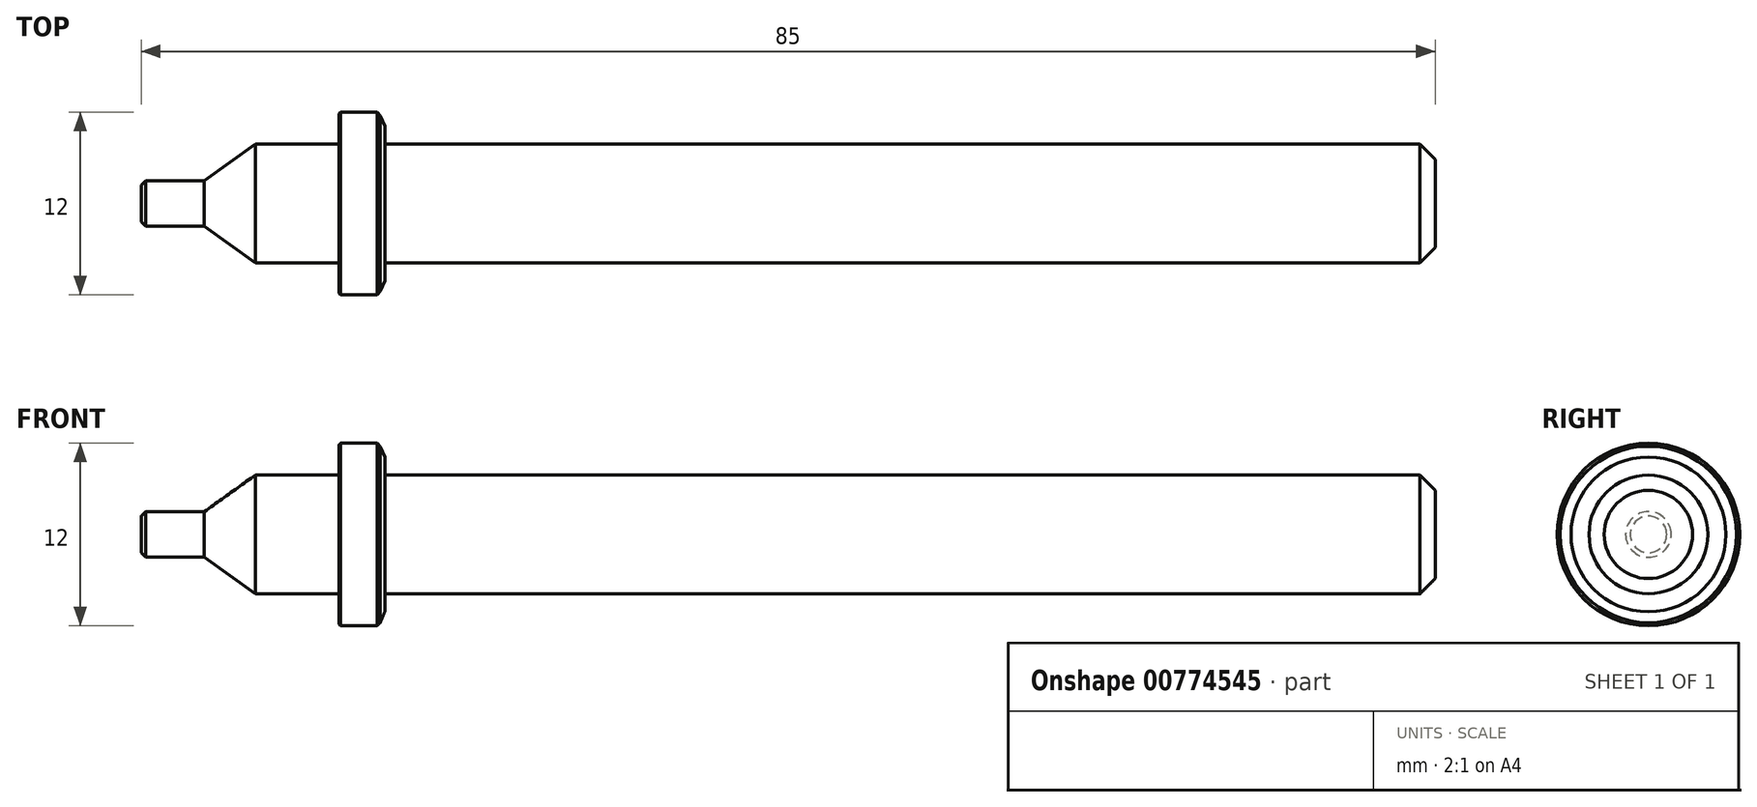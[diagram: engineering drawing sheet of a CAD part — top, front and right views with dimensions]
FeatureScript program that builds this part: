
annotation { "Feature Type Name" : "Feature", "Feature Type Description" : "" }
export const myFeature = defineFeature(function(context is Context, id is Id, definition is map)
    precondition{}
    {
        {
            var Q0;
            Q0=qCreatedBy(makeId("Front.planeOp"),FACE);
            var sketch = newSketch(context, id + "F0", { "sketchPlane" : qUnion([Q0])});
            skLineSegment(sketch, "E0", {"start": v(0, 0) * mm, "end": v(30.28, 0) * mm, "construction": true});
            skLineSegment(sketch, "E1", {"start": v(0, 0) * mm, "end": v(0, 1.5) * mm});
            skLineSegment(sketch, "E2", {"start": v(0, 1.5) * mm, "end": v(4.15, 1.5) * mm});
            skLineSegment(sketch, "E3", {"start": v(4.15, 1.5) * mm, "end": v(7.5, 3.9) * mm});
            skLineSegment(sketch, "E4", {"start": v(7.5, 3.9) * mm, "end": v(13, 3.9) * mm});
            skLineSegment(sketch, "E5", {"start": v(13, 3.9) * mm, "end": v(13, 6) * mm});
            skLineSegment(sketch, "E6", {"start": v(13, 6) * mm, "end": v(16, 6) * mm});
            skLineSegment(sketch, "E7", {"start": v(16, 6) * mm, "end": v(16, 3.9) * mm});
            skLineSegment(sketch, "E8", {"start": v(85, 3.9) * mm, "end": v(85, 0) * mm});
            skLineSegment(sketch, "E9", {"start": v(71, 3.9) * mm, "end": v(71, 0) * mm});
            skLineSegment(sketch, "E10", {"start": v(16, 3.9) * mm, "end": v(71, 3.9) * mm});
            skLineSegment(sketch, "E11", {"start": v(71, 3.9) * mm, "end": v(85, 3.9) * mm});
            skLineSegment(sketch, "E12", {"start": v(0, 0) * mm, "end": v(71, 0) * mm});
            skLineSegment(sketch, "E13", {"start": v(71, 0) * mm, "end": v(85, 0) * mm});
            skSolve(sketch);
        }
        {
            var Q0;
            Q0 = qSketchRegion(id + "F0", true);
            var Q1;
            Q1=sQuery(id+"F0.wireOp",EDGE,"E12");
            revolve(context, id + "F1", {"surfaceOperationType" : NewSurfaceOperationType.NEW, "entities" : qUnion([Q0]), "axis" : qUnion([Q1]), "revolveType" : RevolveType.FULL});
        }
        {
            var Q0;
            Q0=makeQuery(id+"F1.opRevolve","SWEPT_EDGE",EDGE,{"disambiguationData":[OSD([sQuery(id+"F0.wireOp",EDGE,"E6"),sQuery(id+"F0.wireOp",EDGE,"E7")])]});
            chamfer(context, id + "F2", {"entities" : qUnion([Q0]), "width" : 0.5 * mm, "tangentPropagation" : true});
        }
        {
            var Q0;
            Q0=makeQuery(id+"F1.opRevolve","SWEPT_EDGE",EDGE,{"disambiguationData":[OSD([sQuery(id+"F0.wireOp",EDGE,"E5"),sQuery(id+"F0.wireOp",EDGE,"E6")])]});
            chamfer(context, id + "F3", {"entities" : qUnion([Q0]), "width" : 0.1 * mm, "tangentPropagation" : true});
        }
        {
            var Q0;
            Q0=makeQuery(id+"F1.opRevolve","SWEPT_EDGE",EDGE,{"disambiguationData":[OSD([sQuery(id+"F0.wireOp",EDGE,"E1"),sQuery(id+"F0.wireOp",EDGE,"E2")])]});
            chamfer(context, id + "F4", {"entities" : qUnion([Q0]), "width" : 0.3 * mm, "tangentPropagation" : true});
        }
        {
            var Q0;
            Q0=makeQuery(id+"F1.opRevolve","SWEPT_EDGE",EDGE,{"disambiguationData":[OSD([sQuery(id+"F0.wireOp",EDGE,"Cxqr2cfI-QiUm-cGDn-CyId-we9QyebpDtsG"),sQuery(id+"F0.wireOp",EDGE,"E8")])]});
            var Q1;
            {var subQ0=sQuery(id+"F0.wireOp",EDGE,"E7");Q1=makeQuery(id+"F2.opChamfer","BLEND_EDGE",EDGE,{"blendedFrom":[makeQuery(id+"F1.opRevolve","SWEPT_EDGE",EDGE,{"disambiguationData":[OSD([sQuery(id+"F0.wireOp",EDGE,"E6"),subQ0])]}),makeQuery(id+"F1.opRevolve","SWEPT_FACE",FACE,{"disambiguationData":[OSD([subQ0])]})],"blendedInto":[makeQuery(id+"F1.opRevolve","SWEPT_FACE",FACE,{"disambiguationData":[OSD([subQ0])]})]});}
            chamfer(context, id + "F5", {"entities" : qUnion([Q0, Q1]), "width" : 1 * mm, "tangentPropagation" : true});
        }
    });
